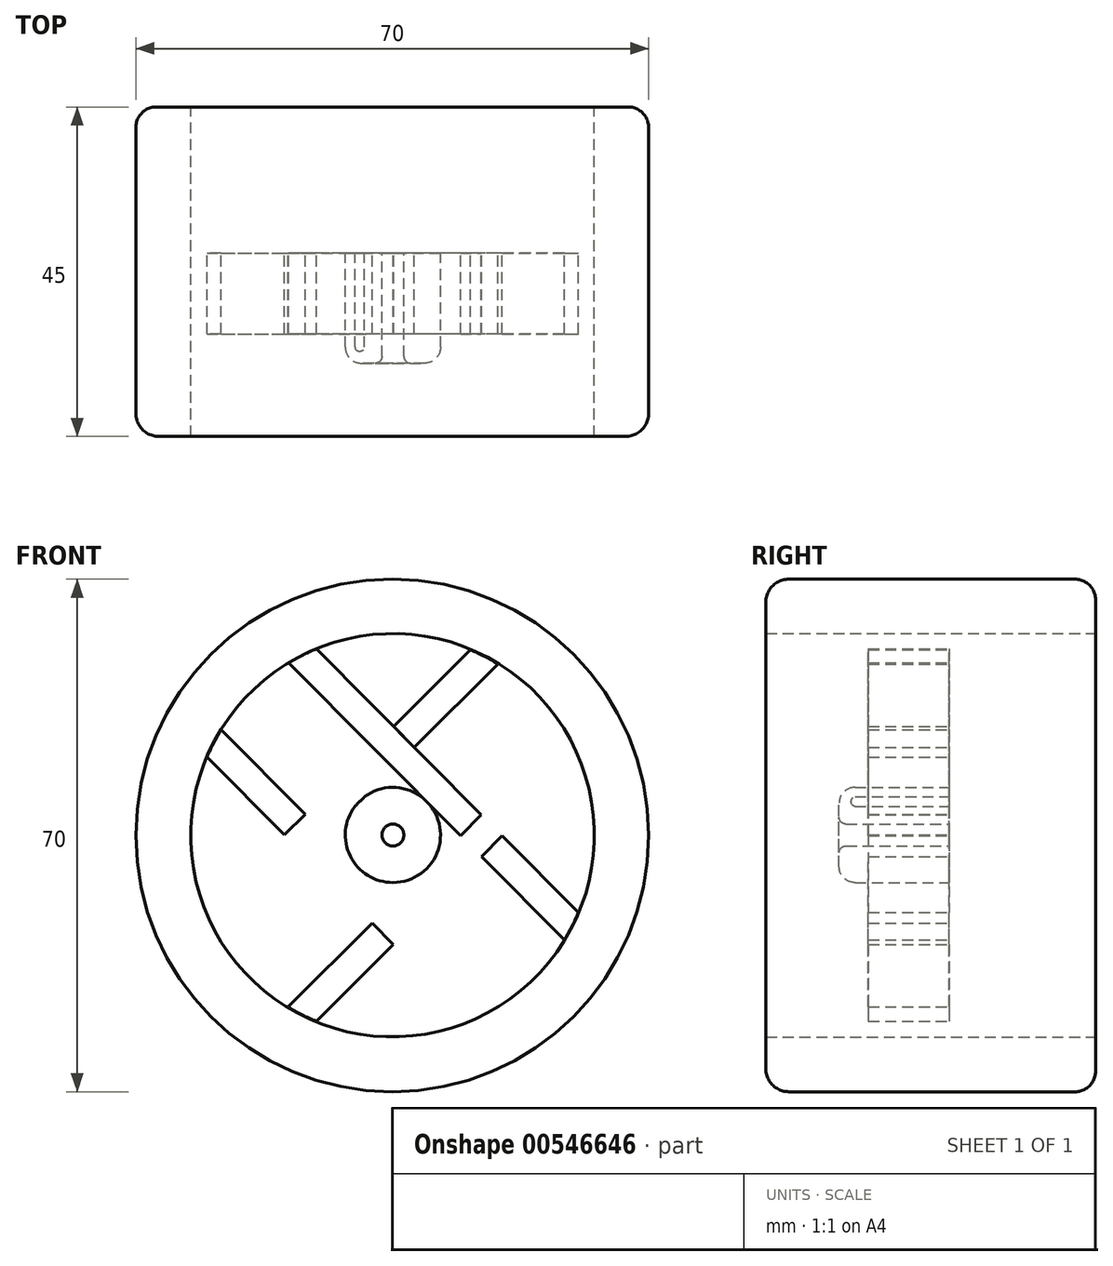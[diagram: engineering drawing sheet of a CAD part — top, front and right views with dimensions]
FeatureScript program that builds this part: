
annotation { "Feature Type Name" : "Feature", "Feature Type Description" : "" }
export const myFeature = defineFeature(function(context is Context, id is Id, definition is map)
    precondition{}
    {
        {
            var Q0;
            Q0=qCreatedBy(makeId("Front.planeOp"),FACE);
            var sketch = newSketch(context, id + "F0", { "sketchPlane" : qUnion([Q0])});
            skCircle(sketch, "E0", {"center": v(0, 0) * mm, "radius": 35 * mm});
            skCircle(sketch, "E1", {"center": v(0, 0) * mm, "radius": 27.5 * mm});
            skCircle(sketch, "E2", {"center": v(0.1, 0.07) * mm, "radius": 27.5 * mm});
            skCircle(sketch, "E3", {"center": v(0.1, 0.07) * mm, "radius": 6.5 * mm});
            skCircle(sketch, "E4", {"center": v(0.1, 0.07) * mm, "radius": 1.5 * mm});
            skLineSegment(sketch, "E5", {"start": v(18.4, -9.13) * mm, "end": v(23.54, -14.3) * mm});
            skLineSegment(sketch, "E6", {"start": v(23.54, -14.3) * mm, "end": v(12.17, -2.86) * mm});
            skLineSegment(sketch, "E7", {"start": v(-14.14, 23.6) * mm, "end": v(-14.16, 23.57) * mm});
            skLineSegment(sketch, "E8", {"start": v(-23.36, 14.43) * mm, "end": v(-11.89, 2.9) * mm});
            skLineSegment(sketch, "E9", {"start": v(14.32, -23.47) * mm, "end": v(9.19, -18.3) * mm});
            skLineSegment(sketch, "E10", {"start": v(6.35, -21.12) * mm, "end": v(10.57, -25.36) * mm});
            skLineSegment(sketch, "E11", {"start": v(10.57, -25.36) * mm, "end": v(-11.9, -2.77) * mm});
            skLineSegment(sketch, "E12", {"start": v(-25.27, 10.69) * mm, "end": v(-14.72, 0.08) * mm});
            skLineSegment(sketch, "E13", {"start": v(21.24, -6.31) * mm, "end": v(25.46, -10.55) * mm});
            skLineSegment(sketch, "E14", {"start": v(25.46, -10.55) * mm, "end": v(15, -0.04) * mm});
            skLineSegment(sketch, "E15", {"start": v(-9.1, -18.32) * mm, "end": v(-14.22, -23.42) * mm});
            skLineSegment(sketch, "E16", {"start": v(-14.22, -23.42) * mm, "end": v(-2.72, -12) * mm});
            skLineSegment(sketch, "E17", {"start": v(14.47, 23.44) * mm, "end": v(3, 12.03) * mm});
            skLineSegment(sketch, "E18", {"start": v(-23.4, -14.22) * mm, "end": v(-18.3, -9.12) * mm});
            skLineSegment(sketch, "E19", {"start": v(-21.12, -6.29) * mm, "end": v(-25.31, -10.46) * mm});
            skLineSegment(sketch, "E20", {"start": v(-25.31, -10.46) * mm, "end": v(-2.67, 12.06) * mm});
            skLineSegment(sketch, "E21", {"start": v(10.69, 25.34) * mm, "end": v(6.52, 21.2) * mm});
            skLineSegment(sketch, "E22", {"start": v(21.34, 6.3) * mm, "end": v(25.46, 10.4) * mm});
            skLineSegment(sketch, "E23", {"start": v(25.46, 10.4) * mm, "end": v(2.98, -12.05) * mm});
            skLineSegment(sketch, "E24.trimOffspring", {"start": v(-9.05, 0.05) * mm, "end": v(14.32, -23.47) * mm});
            skLineSegment(sketch, "E25.trimOffspring", {"start": v(-11.9, -2.77) * mm, "end": v(10.57, -25.36) * mm});
            skLineSegment(sketch, "E26.trimOffspring", {"start": v(-14.72, 0.08) * mm, "end": v(-25.27, 10.69) * mm});
            skLineSegment(sketch, "E27.trimOffspring", {"start": v(9.33, 0) * mm, "end": v(-14.14, 23.6) * mm});
            skLineSegment(sketch, "E28.trimOffspring", {"start": v(12.17, 2.81) * mm, "end": v(-10.38, 25.5) * mm});
            skLineSegment(sketch, "E29.trimOffspring", {"start": v(0.15, -14.88) * mm, "end": v(-10.43, -25.45) * mm});
            skLineSegment(sketch, "E30.trimOffspring", {"start": v(0.11, -9.17) * mm, "end": v(23.66, 14.24) * mm});
            skLineSegment(sketch, "E31.trimOffspring", {"start": v(0.17, 14.88) * mm, "end": v(10.69, 25.34) * mm});
            skLineSegment(sketch, "E32.trimOffspring", {"start": v(0.17, 9.21) * mm, "end": v(-23.4, -14.22) * mm});
            skSolve(sketch);
        }
        {
            var Q0;
            Q0=makeQuery(id+"F0.imprint","IMPRINT",FACE,{"disambiguationData":[TD([[makeQuery(id+"F0.imprint","IMPRINT",EDGE,{"derivedFrom":sQuery(id+"F0.wireOp",EDGE,"E0")}),1.0]])]});
            extrude(context, id + "F1", {"entities" : qUnion([Q0]), "depth" : 20 * mm, "offsetDistance" : 25 * mm});
        }
        {
            var Q0;
            Q0=makeQuery(id+"F1.opExtrude","CAP_FACE",FACE,{"disambiguationData":[OSD([sQuery(id+"F0.wireOp",EDGE,"E0"),sQuery(id+"F0.wireOp",EDGE,"E1")])],"isStart":true});
            extrude(context, id + "F2", {"entities" : qUnion([Q0]), "operationType" : NewBodyOperationType.ADD, "depth" : 20 * mm, "offsetDistance" : 25 * mm});
        }
        {
            var Q0;
            Q0=makeQuery(id+"F1.opExtrude","CAP_EDGE",EDGE,{"disambiguationData":[OSD([sQuery(id+"F0.wireOp",EDGE,"E0")])],"isStart":false});
            fillet(context, id + "F3", {"entities" : qUnion([Q0]), "radius" : 2.8 * mm, "tangentPropagation" : true, "allowEdgeOverflow" : false});
        }
        {
            var Q0;
            Q0=makeQuery(id+"F2.opExtrude","CAP_EDGE",EDGE,{"disambiguationData":[OSD([sQuery(id+"F0.wireOp",EDGE,"E0")])],"isStart":false});
            fillet(context, id + "F4", {"entities" : qUnion([Q0]), "radius" : 2.8 * mm, "tangentPropagation" : true, "allowEdgeOverflow" : false});
        }
        {
            var Q0;
            Q0=makeQuery(id+"F0.imprint","IMPRINT",FACE,{"disambiguationData":[TD([[makeQuery(id+"F0.imprint","IMPRINT",EDGE,{"derivedFrom":sQuery(id+"F0.wireOp",EDGE,"E3")}),1.0]])]});
            extrude(context, id + "F5", {"entities" : qUnion([Q0]), "depth" : 15 * mm, "offsetDistance" : 25 * mm});
        }
        {
            var Q0;
            Q0=makeQuery(id+"F5.opExtrude","CAP_EDGE",EDGE,{"disambiguationData":[OSD([sQuery(id+"F0.wireOp",EDGE,"E3")])],"isStart":false});
            fillet(context, id + "F6", {"entities" : qUnion([Q0]), "radius" : 2.17 * mm, "tangentPropagation" : true, "allowEdgeOverflow" : false});
        }
        {
            var Q0;
            Q0=makeQuery(id+"F5.opExtrude","CAP_EDGE",EDGE,{"disambiguationData":[OSD([sQuery(id+"F0.wireOp",EDGE,"E4")])],"isStart":false});
            fillet(context, id + "F7", {"entities" : qUnion([Q0]), "radius" : 0.92 * mm, "tangentPropagation" : true, "allowEdgeOverflow" : false});
        }
        {
            var Q0;
            Q0 = qSketchRegion(id + "F0", true);
            extrude(context, id + "F8", {"entities" : qUnion([Q0]), "operationType" : NewBodyOperationType.ADD, "depth" : 25 * mm, "offsetDistance" : 25 * mm});
        }
        {
            var Q0;
            {var subQ6=sQuery(id+"F0.wireOp",EDGE,"E20");var subQ14=makeQuery(id+"F0.imprint","IMPRINT",VERTEX,{"derivedFrom":subQ6});Q0=makeQuery(id+"F0.imprint","IMPRINT",FACE,{"disambiguationData":[TD([[makeQuery(id+"F0.imprint","IMPRINT",EDGE,{"disambiguationData":[TD([[subQ14,1.0]])],"derivedFrom":subQ6}),-1.0]])]});}
            var Q1;
            {var subQ0=sQuery(id+"F0.wireOp",EDGE,"E31.trimOffspring");var subQ3=makeQuery(id+"F0.imprint","IMPRINT",VERTEX,{"derivedFrom":subQ0});Q1=makeQuery(id+"F0.imprint","IMPRINT",FACE,{"disambiguationData":[TD([[makeQuery(id+"F0.imprint","IMPRINT",EDGE,{"disambiguationData":[TD([[subQ3,1.0]])],"derivedFrom":subQ0}),-1.0]])]});}
            var Q2;
            {var subQ0=sQuery(id+"F0.wireOp",EDGE,"E23");var subQ3=makeQuery(id+"F0.imprint","IMPRINT",VERTEX,{"derivedFrom":subQ0});Q2=makeQuery(id+"F0.imprint","IMPRINT",FACE,{"disambiguationData":[TD([[makeQuery(id+"F0.imprint","IMPRINT",EDGE,{"disambiguationData":[TD([[subQ3,1.0]])],"derivedFrom":subQ0}),-1.0]])]});}
            var Q3;
            {var subQ0=sQuery(id+"F0.wireOp",EDGE,"E16");Q3=makeQuery(id+"F0.imprint","IMPRINT",FACE,{"disambiguationData":[TD([[makeQuery(id+"F0.imprint","IMPRINT",EDGE,{"derivedFrom":subQ0}),-1.0]])]});}
            extrude(context, id + "F9", {"entities" : qUnion([Q0, Q1, Q2, Q3]), "depth" : 11 * mm, "offsetDistance" : 25 * mm});
        }
        {
            var Q0;
            {var subQ6=sQuery(id+"F0.wireOp",EDGE,"E24.trimOffspring");var subQ11=makeQuery(id+"F0.imprint","IMPRINT",VERTEX,{"derivedFrom":subQ6});Q0=makeQuery(id+"F0.imprint","IMPRINT",FACE,{"disambiguationData":[TD([[makeQuery(id+"F0.imprint","IMPRINT",EDGE,{"disambiguationData":[TD([[subQ11,1.0]])],"derivedFrom":subQ6}),-1.0]])]});}
            var Q1;
            {var subQ0=sQuery(id+"F0.wireOp",EDGE,"E8");Q1=makeQuery(id+"F0.imprint","IMPRINT",FACE,{"disambiguationData":[TD([[makeQuery(id+"F0.imprint","IMPRINT",EDGE,{"derivedFrom":subQ0}),-1.0]])]});}
            var Q2;
            {var subQ6=sQuery(id+"F0.wireOp",EDGE,"E28.trimOffspring");var subQ8=sQuery(id+"F0.wireOp",EDGE,"E1");var subQ9=makeQuery(id+"F0.imprint","INTERSECT",VERTEX,{"derivedFrom":[subQ8,subQ6]});Q2=makeQuery(id+"F0.imprint","IMPRINT",FACE,{"disambiguationData":[TD([[makeQuery(id+"F0.imprint","IMPRINT",EDGE,{"disambiguationData":[TD([[subQ9,-1.0]])],"derivedFrom":subQ8}),1.0]])]});}
            var Q3;
            {var subQ1=sQuery(id+"F0.wireOp",EDGE,"E6");var subQ3=makeQuery(id+"F0.imprint","IMPRINT",VERTEX,{"derivedFrom":subQ1});Q3=makeQuery(id+"F0.imprint","IMPRINT",FACE,{"disambiguationData":[TD([[makeQuery(id+"F0.imprint","IMPRINT",EDGE,{"disambiguationData":[TD([[subQ3,1.0]])],"derivedFrom":subQ1}),-1.0]])]});}
            extrude(context, id + "F10", {"entities" : qUnion([Q0, Q1, Q2, Q3]), "depth" : 11 * mm, "offsetDistance" : 25 * mm});
        }
        {
            var Q0;
            Q0=makeQuery(id+"F8.opExtrude","CAP_EDGE",EDGE,{"disambiguationData":[OSD([sQuery(id+"F0.wireOp",EDGE,"E0")])],"isStart":false});
            fillet(context, id + "F11", {"entities" : qUnion([Q0]), "radius" : 3.14 * mm, "tangentPropagation" : true, "allowEdgeOverflow" : false});
        }
    });
